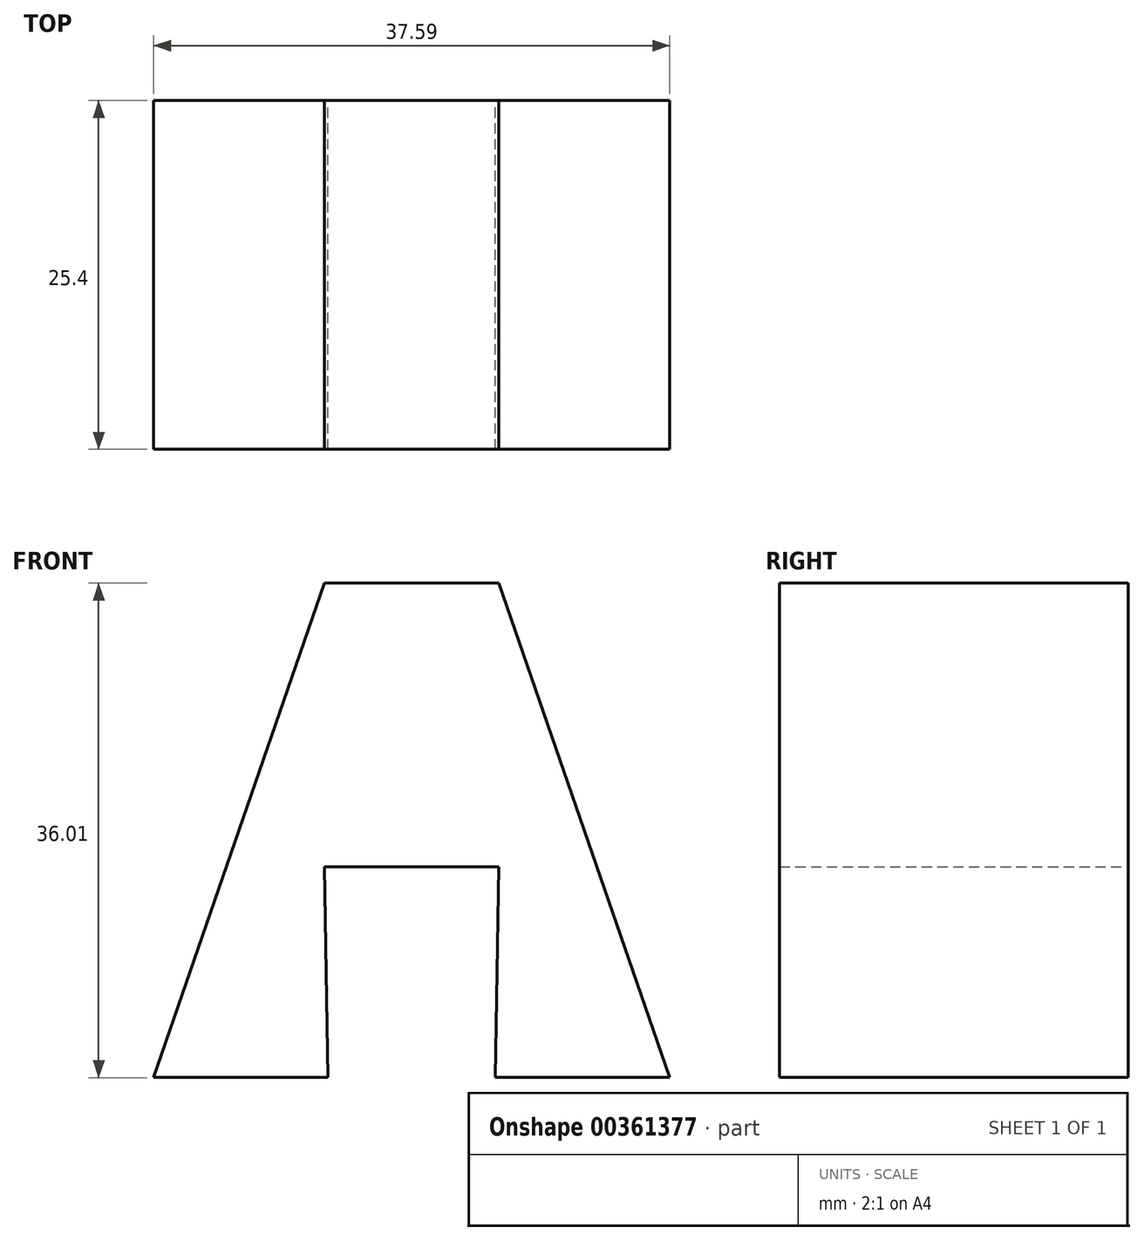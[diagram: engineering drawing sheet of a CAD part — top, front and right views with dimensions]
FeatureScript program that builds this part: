
annotation { "Feature Type Name" : "Feature", "Feature Type Description" : "" }
export const myFeature = defineFeature(function(context is Context, id is Id, definition is map)
    precondition{}
    {
        {
            var Q0;
            Q0=qCreatedBy(makeId("Front.planeOp"),FACE);
            var sketch = newSketch(context, id + "F0", { "sketchPlane" : qUnion([Q0])});
            skLineSegment(sketch, "E0", {"start": v(-65.92, 6.23) * mm, "end": v(-53.48, 42.24) * mm});
            skLineSegment(sketch, "E1", {"start": v(-53.48, 42.24) * mm, "end": v(-40.78, 42.24) * mm});
            skLineSegment(sketch, "E2", {"start": v(-40.78, 42.24) * mm, "end": v(-28.33, 6.23) * mm});
            skLineSegment(sketch, "E3", {"start": v(-28.33, 6.23) * mm, "end": v(-41.03, 6.23) * mm});
            skLineSegment(sketch, "E4", {"start": v(-41.03, 6.23) * mm, "end": v(-40.78, 21.6) * mm});
            skLineSegment(sketch, "E5", {"start": v(-40.78, 21.6) * mm, "end": v(-53.48, 21.6) * mm});
            skLineSegment(sketch, "E6", {"start": v(-53.48, 21.6) * mm, "end": v(-53.22, 6.23) * mm});
            skLineSegment(sketch, "E7", {"start": v(-53.22, 6.23) * mm, "end": v(-65.92, 6.23) * mm});
            skSolve(sketch);
        }
        {
            var Q0;
            Q0 = qSketchRegion(id + "F0", true);
            extrude(context, id + "F1", {"entities" : qUnion([Q0]), "depth" : 25.4 * mm});
        }
    });
